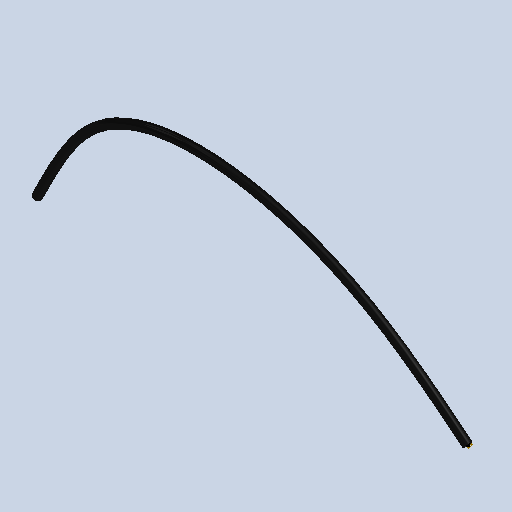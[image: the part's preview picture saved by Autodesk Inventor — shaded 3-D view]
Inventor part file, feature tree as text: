
AUTODESK INVENTOR PART (.ipt)
format: ipt  version: 2023.1 (Build 271208000, 208)  size: 91,648 bytes
history: native  units: mm (DEFAULTED — no unit token found)
features: other x6, plane x1, sketch x1, sweep x1
ambient origin geometry x8: Origin, YZ Plane, XZ Plane, XY Plane, X Axis, Y Axis, Z Axis, Center Point
bodies: Body1 (feature_tree)
feature tree (9):
  other  "Work Point9"
  other  "Work Point10"
  other  "Cable1:1"
  plane  "Work Plane3"
  other  "Work Point11"
  other  "Work Point12"
  sketch  "Sketch3"  dims[d4=0.0mm d5=0.0mm]
  other  "Srf3"
  sweep  "SweepSrf3"
